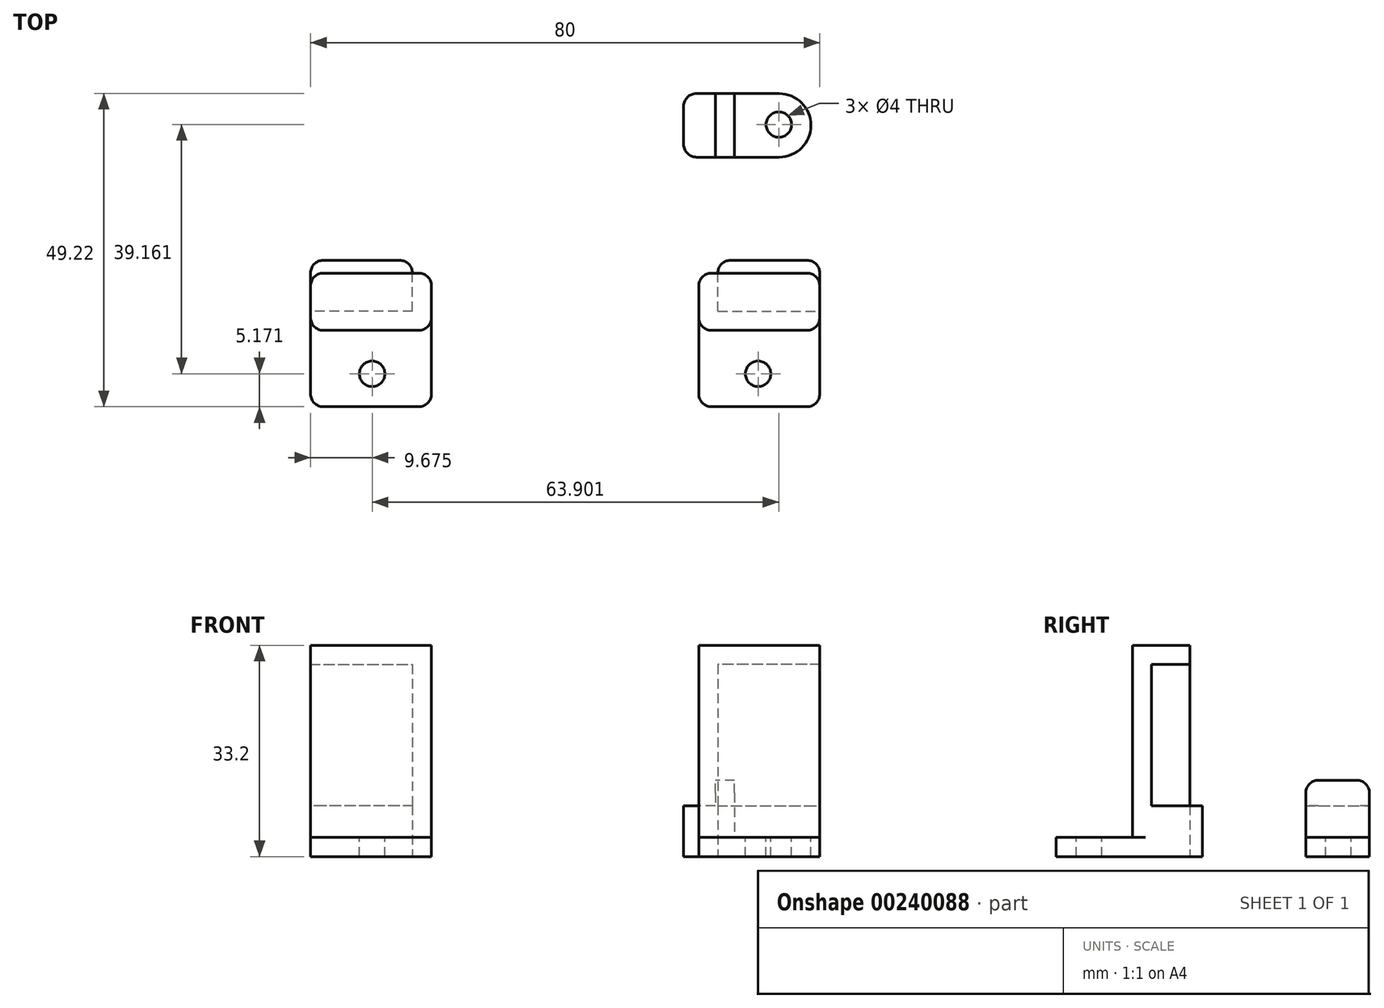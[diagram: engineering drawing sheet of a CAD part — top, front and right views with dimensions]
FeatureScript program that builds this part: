
annotation { "Feature Type Name" : "Feature", "Feature Type Description" : "" }
export const myFeature = defineFeature(function(context is Context, id is Id, definition is map)
    precondition{}
    {
        {
            var Q0;
            Q0=qCreatedBy(makeId("Top.planeOp"),FACE);
            var sketch = newSketch(context, id + "F0", { "sketchPlane" : qUnion([Q0])});
            skLineSegment(sketch, "E0", {"start": v(-69.9, 0) * mm, "end": v(79.98, 0) * mm, "construction": true});
            skLineSegment(sketch, "E1", {"start": v(0, 59.98) * mm, "end": v(0, -61.02) * mm, "construction": true});
            skLineSegment(sketch, "E2.bottom", {"start": v(0, 0) * mm, "end": v(-16, 0) * mm});
            skLineSegment(sketch, "E2.top", {"start": v(0, 8) * mm, "end": v(-16, 8) * mm});
            skLineSegment(sketch, "E2.left", {"start": v(0, 0) * mm, "end": v(0, 8) * mm});
            skLineSegment(sketch, "E2.right", {"start": v(-16, 0) * mm, "end": v(-16, 8) * mm});
            skSolve(sketch);
        }
        {
            var Q0;
            Q0=qSketchRegion(id+"F0",true);
            extrude(context, id + "F1", {"entities" : qUnion([Q0]), "depth" : 8 * mm});
        }
        {
            var Q0;
            Q0=qCreatedBy(makeId("Top.planeOp"),FACE);
            var sketch = newSketch(context, id + "F2", { "sketchPlane" : qUnion([Q0])});
            skLineSegment(sketch, "E3.bottom", {"start": v(0, 0) * mm, "end": v(-16, 0) * mm});
            skLineSegment(sketch, "E3.top", {"start": v(0, -3) * mm, "end": v(-16, -3) * mm});
            skLineSegment(sketch, "E3.left", {"start": v(0, 0) * mm, "end": v(0, -3) * mm});
            skLineSegment(sketch, "E3.right", {"start": v(-16, 0) * mm, "end": v(-16, -3) * mm});
            skLineSegment(sketch, "E4.bottom", {"start": v(0, -3) * mm, "end": v(3, -3) * mm});
            skLineSegment(sketch, "E4.top", {"start": v(0, 6) * mm, "end": v(3, 6) * mm});
            skLineSegment(sketch, "E4.left", {"start": v(0, -3) * mm, "end": v(0, 6) * mm});
            skLineSegment(sketch, "E4.right", {"start": v(3, -3) * mm, "end": v(3, 6) * mm});
            skSolve(sketch);
        }
        {
            var Q0;
            Q0=qSketchRegion(id+"F2",true);
            extrude(context, id + "F3", {"entities" : qUnion([Q0]), "operationType" : NewBodyOperationType.ADD, "depth" : 33.2 * mm});
        }
        {
            var Q0;
            Q0=makeQuery(id+"F3.opExtrude","SWEPT_FACE",FACE,{"disambiguationData":[OSD([sQuery(id+"F2.wireOp",EDGE,"E3.top"),sQuery(id+"F2.wireOp",EDGE,"E4.bottom")])]});
            var sketch = newSketch(context, id + "F4", { "sketchPlane" : qUnion([Q0])});
            skLineSegment(sketch, "E5.bottom", {"start": v(-16, 0) * mm, "end": v(3, 0) * mm});
            skLineSegment(sketch, "E5.top", {"start": v(-16, 3) * mm, "end": v(3, 3) * mm});
            skLineSegment(sketch, "E5.left", {"start": v(-16, 0) * mm, "end": v(-16, 3) * mm});
            skLineSegment(sketch, "E5.right", {"start": v(3, 0) * mm, "end": v(3, 3) * mm});
            skSolve(sketch);
        }
        {
            var Q0;
            Q0=qSketchRegion(id+"F4",true);
            extrude(context, id + "F5", {"entities" : qUnion([Q0]), "operationType" : NewBodyOperationType.ADD, "depth" : 12 * mm});
        }
        {
            var Q0;
            Q0=makeQuery(id+"F5.opExtrude","SWEPT_FACE",FACE,{"disambiguationData":[OSD([sQuery(id+"F4.wireOp",EDGE,"E5.top")])]});
            var sketch = newSketch(context, id + "F6", { "sketchPlane" : qUnion([Q0])});
            skCircle(sketch, "E6", {"center": v(-6.32, -9.83) * mm, "radius": 2 * mm});
            skSolve(sketch);
        }
        {
            var Q0;
            Q0=qSketchRegion(id+"F6",true);
            var Q1;
            Q1=makeQuery(id+"F5.boolean.opBoolean","MERGE",FACE,{"derivedFrom":[makeQuery(id+"F3.boolean.opBoolean","MERGE",FACE,{"derivedFrom":[makeQuery(id+"F1.opExtrude","CAP_FACE",FACE,{"disambiguationData":[OSD([sQuery(id+"F0.wireOp",EDGE,"E2.bottom"),sQuery(id+"F0.wireOp",EDGE,"E2.top"),sQuery(id+"F0.wireOp",EDGE,"E2.left"),sQuery(id+"F0.wireOp",EDGE,"E2.right")])],"isStart":true}),makeQuery(id+"F3.opExtrude","CAP_FACE",FACE,{"disambiguationData":[OSD([sQuery(id+"F2.wireOp",EDGE,"E3.bottom"),sQuery(id+"F2.wireOp",EDGE,"E3.top"),sQuery(id+"F2.wireOp",EDGE,"E3.right"),sQuery(id+"F2.wireOp",EDGE,"E4.bottom"),sQuery(id+"F2.wireOp",EDGE,"E4.top"),sQuery(id+"F2.wireOp",EDGE,"E4.left"),sQuery(id+"F2.wireOp",EDGE,"E4.right")])],"isStart":true})]}),makeQuery(id+"F5.opExtrude","SWEPT_FACE",FACE,{"disambiguationData":[OSD([sQuery(id+"F4.wireOp",EDGE,"E5.bottom")])]})]});
            extrude(context, id + "F7", {"entities" : qUnion([Q0]), "operationType" : NewBodyOperationType.REMOVE, "endBound" : BoundingType.UP_TO_SURFACE, "oppositeDirection" : true, "endBoundEntityFace" : qUnion([Q1]), "depth" : 25 * mm});
        }
        {
            var Q0;
            Q0=makeQuery(id+"F3.opExtrude","SWEPT_FACE",FACE,{"disambiguationData":[OSD([sQuery(id+"F2.wireOp",EDGE,"E3.bottom")])]});
            var sketch = newSketch(context, id + "F8", { "sketchPlane" : qUnion([Q0])});
            skLineSegment(sketch, "E7.bottom", {"start": v(16, 33.2) * mm, "end": v(0, 33.2) * mm});
            skLineSegment(sketch, "E7.top", {"start": v(16, 30.2) * mm, "end": v(0, 30.2) * mm});
            skLineSegment(sketch, "E7.left", {"start": v(16, 33.2) * mm, "end": v(16, 30.2) * mm});
            skLineSegment(sketch, "E7.right", {"start": v(0, 33.2) * mm, "end": v(0, 30.2) * mm});
            skSolve(sketch);
        }
        {
            var Q0;
            Q0=qSketchRegion(id+"F8",true);
            extrude(context, id + "F9", {"entities" : qUnion([Q0]), "operationType" : NewBodyOperationType.ADD, "depth" : 6 * mm});
        }
        {
            var Q0;
            Q0=makeQuery(id+"F9.opExtrude","CAP_EDGE",EDGE,{"disambiguationData":[OSD([sQuery(id+"F8.wireOp",EDGE,"E7.left")])],"isStart":false});
            var Q1;
            Q1=makeQuery(id+"F1.opExtrude","SWEPT_EDGE",EDGE,{"disambiguationData":[OSD([sQuery(id+"F0.wireOp",EDGE,"E2.top"),sQuery(id+"F0.wireOp",EDGE,"E2.right")])]});
            var Q2;
            Q2=makeQuery(id+"F1.opExtrude","SWEPT_EDGE",EDGE,{"disambiguationData":[OSD([sQuery(id+"F0.wireOp",EDGE,"E2.top"),sQuery(id+"F0.wireOp",EDGE,"E2.left")])]});
            var Q3;
            Q3=makeQuery(id+"F3.opExtrude","SWEPT_EDGE",EDGE,{"disambiguationData":[OSD([sQuery(id+"F2.wireOp",EDGE,"E4.top"),sQuery(id+"F2.wireOp",EDGE,"E4.right")])]});
            var Q4;
            Q4=makeQuery(id+"F5.opExtrude","CAP_EDGE",EDGE,{"disambiguationData":[OSD([sQuery(id+"F4.wireOp",EDGE,"E5.right")])],"isStart":false});
            var Q5;
            Q5=makeQuery(id+"F3.opExtrude","SWEPT_EDGE",EDGE,{"disambiguationData":[OSD([sQuery(id+"F2.wireOp",EDGE,"E4.bottom"),sQuery(id+"F2.wireOp",EDGE,"E4.right")])]});
            var Q6;
            Q6=makeQuery(id+"F3.opExtrude","SWEPT_EDGE",EDGE,{"disambiguationData":[OSD([sQuery(id+"F2.wireOp",EDGE,"E3.top"),sQuery(id+"F2.wireOp",EDGE,"E3.right")])]});
            var Q7;
            Q7=makeQuery(id+"F5.opExtrude","CAP_EDGE",EDGE,{"disambiguationData":[OSD([sQuery(id+"F4.wireOp",EDGE,"E5.left")])],"isStart":false});
            fillet(context, id + "F10", {"entities" : qUnion([Q0, Q1, Q2, Q3, Q4, Q5, Q6, Q7]), "radius" : 2 * mm, "tangentPropagation" : true, "allowEdgeOverflow" : false});
        }
        {
            var Q0;
            Q0=qCreatedBy(makeId("Right.planeOp"),FACE);
            cPlane(context, id + "F11", {"entities" : qUnion([Q0]), "cplaneType" : CPlaneType.OFFSET, "offset" : 24 * mm, "width" : 150 * mm, "height" : 150 * mm});
        }
        {
            var Q0;
            Q0=makeQuery(id+"F1.opExtrude","SWEPT_BODY",BODY,{"disambiguationData":[OSD([sQuery(id+"F0.wireOp",EDGE,"E2.bottom"),sQuery(id+"F0.wireOp",EDGE,"E2.top"),sQuery(id+"F0.wireOp",EDGE,"E2.left"),sQuery(id+"F0.wireOp",EDGE,"E2.right")])]});
            var Q1;
            Q1=qCreatedBy(id+"F11.planeOp",FACE);
            mirror(context, id + "F12", {"entities" : qUnion([Q0]), "mirrorPlane" : qUnion([Q1])});
        }
        {
            var Q0;
            Q0=qCreatedBy(makeId("Top.planeOp"),FACE);
            var sketch = newSketch(context, id + "F13", { "sketchPlane" : qUnion([Q0])});
            skLineSegment(sketch, "E8.bottom", {"start": v(50.62, 24.22) * mm, "end": v(42.62, 24.22) * mm});
            skLineSegment(sketch, "E8.top", {"start": v(50.62, 34.22) * mm, "end": v(42.62, 34.22) * mm});
            skLineSegment(sketch, "E8.left", {"start": v(50.62, 24.22) * mm, "end": v(50.62, 34.22) * mm});
            skLineSegment(sketch, "E8.right", {"start": v(42.62, 24.22) * mm, "end": v(42.62, 34.22) * mm});
            skSolve(sketch);
        }
        {
            var Q0;
            Q0 = qSketchRegion(id + "F13", true);
            extrude(context, id + "F14", {"entities" : qUnion([Q0]), "depth" : 8 * mm});
        }
        {
            var Q0;
            Q0=makeQuery(id+"F14.opExtrude","SWEPT_FACE",FACE,{"disambiguationData":[OSD([sQuery(id+"F13.wireOp",EDGE,"E8.left")])]});
            var sketch = newSketch(context, id + "F15", { "sketchPlane" : qUnion([Q0])});
            skLineSegment(sketch, "E9.bottom", {"start": v(24.22, 0) * mm, "end": v(34.22, 0) * mm});
            skLineSegment(sketch, "E9.top", {"start": v(24.22, 3) * mm, "end": v(34.22, 3) * mm});
            skLineSegment(sketch, "E9.left", {"start": v(24.22, 0) * mm, "end": v(24.22, 3) * mm});
            skLineSegment(sketch, "E9.right", {"start": v(34.22, 0) * mm, "end": v(34.22, 3) * mm});
            skSolve(sketch);
        }
        {
            var Q0;
            Q0 = qSketchRegion(id + "F15", true);
            extrude(context, id + "F16", {"entities" : qUnion([Q0]), "operationType" : NewBodyOperationType.ADD, "depth" : 12 * mm});
        }
        {
            var Q0;
            Q0=makeQuery(id+"F14.opExtrude","CAP_FACE",FACE,{"disambiguationData":[OSD([sQuery(id+"F13.wireOp",EDGE,"E8.bottom"),sQuery(id+"F13.wireOp",EDGE,"E8.top"),sQuery(id+"F13.wireOp",EDGE,"E8.left"),sQuery(id+"F13.wireOp",EDGE,"E8.right")])],"isStart":false});
            var sketch = newSketch(context, id + "F17", { "sketchPlane" : qUnion([Q0])});
            skLineSegment(sketch, "E10.bottom", {"start": v(50.62, 24.22) * mm, "end": v(47.62, 24.22) * mm});
            skLineSegment(sketch, "E10.top", {"start": v(50.62, 34.22) * mm, "end": v(47.62, 34.22) * mm});
            skLineSegment(sketch, "E10.left", {"start": v(50.62, 24.22) * mm, "end": v(50.62, 34.22) * mm});
            skLineSegment(sketch, "E10.right", {"start": v(47.62, 24.22) * mm, "end": v(47.62, 34.22) * mm});
            skSolve(sketch);
        }
        {
            var Q0;
            Q0 = qSketchRegion(id + "F17", true);
            extrude(context, id + "F18", {"entities" : qUnion([Q0]), "operationType" : NewBodyOperationType.ADD, "depth" : 4 * mm});
        }
        {
            var Q0;
            Q0=makeQuery(id+"F16.opExtrude","SWEPT_FACE",FACE,{"disambiguationData":[OSD([sQuery(id+"F15.wireOp",EDGE,"E9.top")])]});
            var sketch = newSketch(context, id + "F19", { "sketchPlane" : qUnion([Q0])});
            skCircle(sketch, "E11", {"center": v(57.58, 29.33) * mm, "radius": 2 * mm});
            skSolve(sketch);
        }
        {
            var Q0;
            Q0 = qSketchRegion(id + "F19", true);
            var Q1;
            Q1=makeQuery(id+"F16.boolean.opBoolean","MERGE",FACE,{"derivedFrom":[makeQuery(id+"F14.opExtrude","CAP_FACE",FACE,{"disambiguationData":[OSD([sQuery(id+"F13.wireOp",EDGE,"E8.bottom"),sQuery(id+"F13.wireOp",EDGE,"E8.top"),sQuery(id+"F13.wireOp",EDGE,"E8.left"),sQuery(id+"F13.wireOp",EDGE,"E8.right")])],"isStart":true}),makeQuery(id+"F16.opExtrude","SWEPT_FACE",FACE,{"disambiguationData":[OSD([sQuery(id+"F15.wireOp",EDGE,"E9.bottom")])]})]});
            extrude(context, id + "F20", {"entities" : qUnion([Q0]), "operationType" : NewBodyOperationType.REMOVE, "endBound" : BoundingType.UP_TO_SURFACE, "oppositeDirection" : true, "endBoundEntityFace" : qUnion([Q1]), "depth" : 25 * mm});
        }
        {
            var Q0;
            Q0=makeQuery(id+"F16.opExtrude","CAP_EDGE",EDGE,{"disambiguationData":[OSD([sQuery(id+"F15.wireOp",EDGE,"E9.right")])],"isStart":false});
            var Q1;
            Q1=makeQuery(id+"F16.opExtrude","CAP_EDGE",EDGE,{"disambiguationData":[OSD([sQuery(id+"F15.wireOp",EDGE,"E9.left")])],"isStart":false});
            fillet(context, id + "F21", {"entities" : qUnion([Q0, Q1]), "radius" : 5 * mm, "tangentPropagation" : true, "allowEdgeOverflow" : false});
        }
        {
            var Q0;
            Q0=makeQuery(id+"F16.opExtrude","CAP_EDGE",EDGE,{"disambiguationData":[OSD([sQuery(id+"F15.wireOp",EDGE,"E9.top")])],"isStart":true});
            var Q1;
            Q1=makeQuery(id+"F18.opExtrude","CAP_EDGE",EDGE,{"disambiguationData":[OSD([sQuery(id+"F17.wireOp",EDGE,"E10.top")])],"isStart":false});
            var Q2;
            Q2=makeQuery(id+"F18.opExtrude","CAP_EDGE",EDGE,{"disambiguationData":[OSD([sQuery(id+"F17.wireOp",EDGE,"E10.bottom")])],"isStart":false});
            var Q3;
            Q3=makeQuery(id+"F14.opExtrude","SWEPT_EDGE",EDGE,{"disambiguationData":[OSD([sQuery(id+"F13.wireOp",EDGE,"E8.top"),sQuery(id+"F13.wireOp",EDGE,"E8.right")])]});
            var Q4;
            Q4=makeQuery(id+"F14.opExtrude","SWEPT_EDGE",EDGE,{"disambiguationData":[OSD([sQuery(id+"F13.wireOp",EDGE,"E8.bottom"),sQuery(id+"F13.wireOp",EDGE,"E8.right")])]});
            fillet(context, id + "F22", {"entities" : qUnion([Q0, Q1, Q2, Q3, Q4]), "radius" : 2 * mm, "tangentPropagation" : true, "allowEdgeOverflow" : false});
        }
    });
